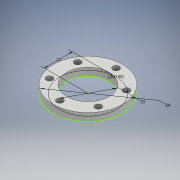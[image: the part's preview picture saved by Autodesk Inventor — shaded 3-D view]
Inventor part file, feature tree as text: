
AUTODESK INVENTOR PART (.ipt)
format: ipt  version: 2019.3 (Build 233278000, 278)  size: 121,344 bytes
history: native  units: mm
features: other x1, sketch x1, extrude x1, hole x1
ambient origin geometry x8: Origin, YZ Plane, XZ Plane, XY Plane, X Axis, Y Axis, Z Axis, Center Point
bodies: Body1 (feature_tree)
feature tree (4):
  other  "SprocketHubPlate"
  sketch  "Sketch1"  dims[d9=33.0mm d20=22.0mm d21=60.0mm d23=360.0deg d30=6.0mm d31=0.0mm d39=5.0mm d40=6.0mm d41=4.0mm d42=2.0mm d43=90.0deg d44=8.0mm d45=20.594885mm d46=62.0mm d58=54.0mm d12=1.0mm d13=1.0mm]
  extrude  "Extrusion2"  Depth=6.0mm
  hole  "Hole3"  [1 undecoded]
note: 1 required parameter value undecoded (feature->parameter linkage not recoverable at this tier; creation-order binding heuristic only, values carry confidence <= 0.55)
